# Revit family: IS_Connect_T9808_BIM_FR
name_source: partatom
category: Plumbing Fixtures
revit_build: Autodesk Revit 2017 (Build: 20160225_1515(x64)
units: mm (PartAtom-declared; Revit-internal decimal feet)

## family parameters
Always vertical = Yes
Cut with Voids When Loaded = No
OmniClass Number = 23.45.05.14.21.11
OmniClass Title = Bath/Shower Units
Part Type = Normal
Room Calculation Point = No
Round Connector Dimension = Use Diameter
Shared = No
Work Plane-Based = No

## types (2) — shared parameters
Accessoires = www.idealspec.fr
Auteur = Ideal Standard
BOSUseNativeGeometries = 1
Bim-NomDuProjet = ISI_IdealStandard_ShowerEnclosures_Connect_T9808
Caractéristiques = CONNECT Porte de douche 100 cm verre transparent
CodeBarre = 8014140381563
Conformité = NF
ConseilsDInstallation = 0
Couleur = clair
DateDeCréation = 2018_08_03
Description = CONNECT Porte de douche 100 cm verre transparent
Dimensions = 1903 x 1020 x 1020mm
EAN code = https://8014140381563
Espace = Interne
Finition = clair
Forme = rectangulaire
Hauteur = 1903 mm
IfcExportAs = Shower enclosures
IfcExportType = IfcSanitaryTerminalType
InformationsProduit = www.idealspec.fr
Largeur = 1020 mm  [stored 3.34646 ft]
Longueur = 1020 mm  [stored 3.34646 ft]
Marque = Ideal Standard
Matériel = Glass
Nom = ShowerEnclosures_Connect_T9808_IdealStandard
PoidsNet = 23,00 KG
Raccordement = Plomberie
Receveur = No
Révision = 1
URL = www.idealspec.fr
Uniclass2015Code = Pr_40_20_06_79
Uniclass2015Title = Shower enclosures
Uniclass2015Version = Products v1.1
UnitéDeMesure = Millimètres
UnitéDeTemps = An
UnitéMonétaire = €
UrlDuFabricant = www.idealspec.fr
Version = 1
zero-valued in all types: Cost, CoûtDeRemplacement, DiamètreÉvacuation, Profondeur

## per-type parameters (varying)
| type | Model |
| T9808EO - CONNECT PAROI ANGLE 100 TSP ARG BR IC | T9808EO |
| T9808AC - CONNECT PAROI ANGLE 100 TSP BLC IC | T9808AC |

note: [stored X ft] marks values corroborated as IEEE doubles in the binary element streams (Revit-internal decimal feet)

## geometry (parser evidence)
native form markers: Sweep x5
no freeform markers — native parametric forms only
